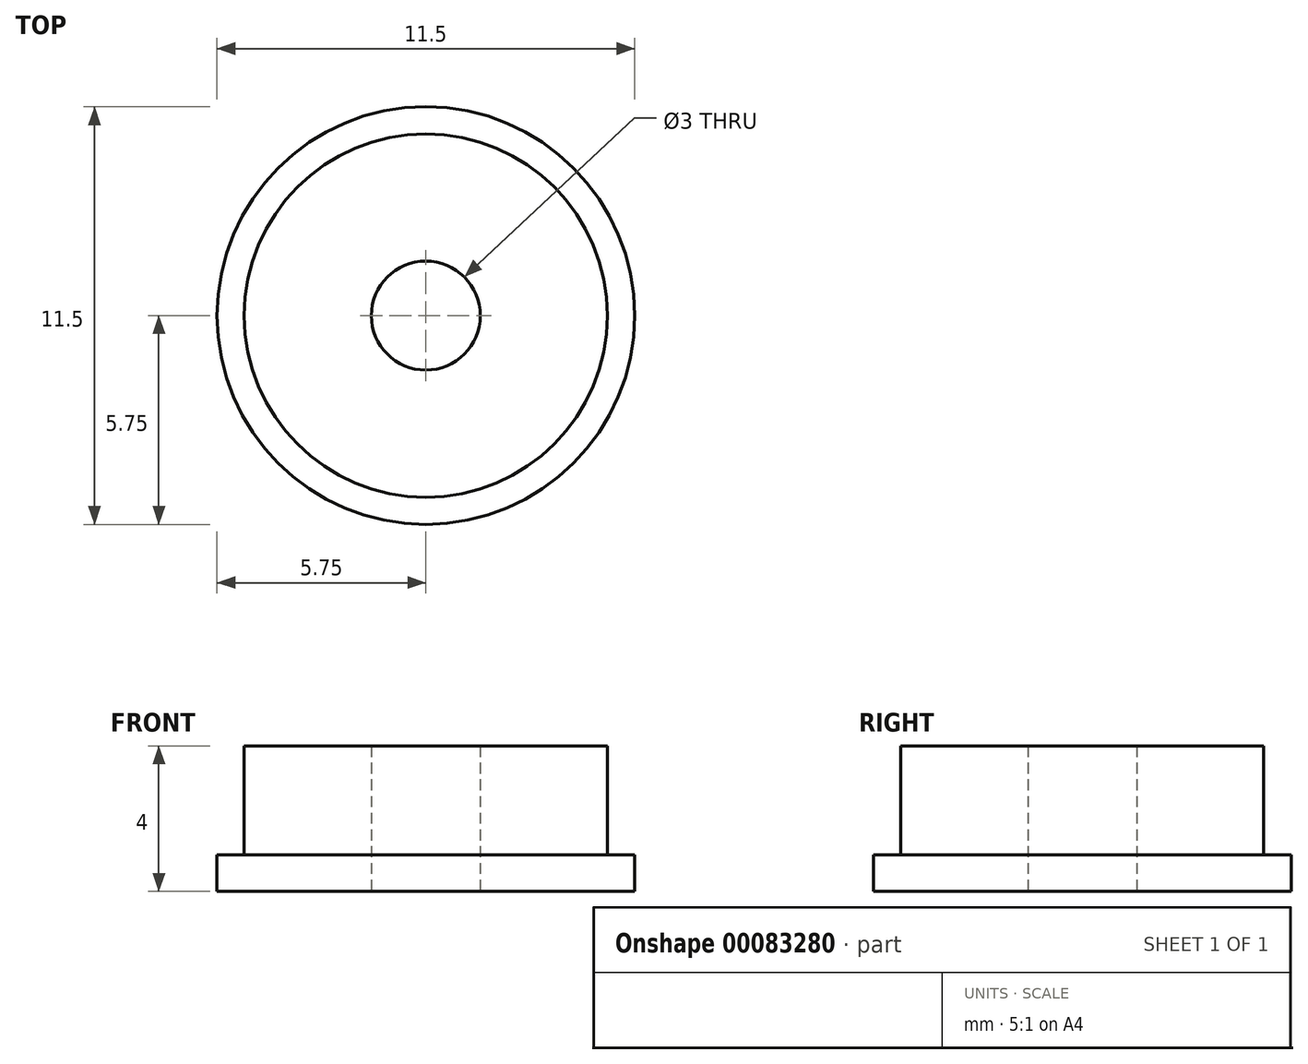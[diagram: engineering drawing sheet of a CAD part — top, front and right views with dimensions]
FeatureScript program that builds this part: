
annotation { "Feature Type Name" : "Feature", "Feature Type Description" : "" }
export const myFeature = defineFeature(function(context is Context, id is Id, definition is map)
    precondition{}
    {
        {
            var Q0;
            Q0=qCreatedBy(makeId("Top.planeOp"),FACE);
            var sketch = newSketch(context, id + "F0", { "sketchPlane" : qUnion([Q0])});
            skCircle(sketch, "E0", {"center": v(0, 0) * mm, "radius": 1.5 * mm});
            skCircle(sketch, "E1", {"center": v(0, 0) * mm, "radius": 5 * mm});
            skCircle(sketch, "E2", {"center": v(0, 0) * mm, "radius": 5.75 * mm});
            skSolve(sketch);
        }
        {
            var Q0;
            Q0=makeQuery(id+"F0.imprint","IMPRINT",FACE,{"disambiguationData":[TD([[makeQuery(id+"F0.imprint","IMPRINT",EDGE,{"derivedFrom":sQuery(id+"F0.wireOp",EDGE,"E0")}),-1.0]])]});
            extrude(context, id + "F1", {"entities" : qUnion([Q0]), "depth" : 4 * mm});
        }
        {
            var Q0;
            Q0 = qSketchRegion(id + "F0", true);
            extrude(context, id + "F2", {"entities" : qUnion([Q0]), "operationType" : NewBodyOperationType.ADD, "depth" : 1 * mm});
        }
    });
